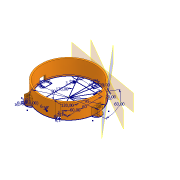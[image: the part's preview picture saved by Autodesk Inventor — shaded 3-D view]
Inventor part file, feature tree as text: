
AUTODESK INVENTOR PART (.ipt)
format: ipt  version: 2020.3 (Build 243373000, 373)  size: 265,216 bytes
history: native  units: mm
features: extrude x8, sketch x5, plane x3
ambient origin geometry x8: Origin, YZ Plane, XZ Plane, XY Plane, X Axis, Y Axis, Z Axis, Center Point
bodies: Body1 (feature_tree)
feature tree (16):
  sketch  "Sketch1"  dims[d0=95.0mm d1=120.0deg]
  extrude  "Extrusion9"  TaperAngle=120.0deg  [1 undecoded]
  extrude  "Extrusion13"  Depth=16.0mm
  extrude  "Extrusion14"  Depth=6.5mm
  extrude  "Extrusion16"  Depth=10.0mm
  extrude  "Extrusion17"  Depth=10.0mm
  plane  "Work Plane5"
  plane  "Work Plane6"
  plane  "Work Plane7"
  sketch  "Sketch12"  dims[d4=3.4mm d5=6.5mm]
  sketch  "Sketch13"  dims[d7=10.0mm d8=3.6mm]
  sketch  "Sketch14"  dims[d9=2.4mm d10=1.2mm d13=30.0mm d15=360.0deg d17=9.8mm d18=12.0mm d19=2.0mm d20=6.0mm d21=2.0mm d23=60.0deg d24=6.1mm d25=8.0mm d26=6.1mm d27=60.0deg d28=3.490659mm d29=3.490659mm d56=40.0mm d57=60.0mm d58=3.2mm d59=1.3mm d60=1.0mm d61=1.0mm d62=1.3mm d64=3.0mm d65=8.0mm d66=6.0mm d74=90.0mm d75=26.0mm d76=0.0mm d83=4.2mm d84=0.0mm d85=8.4mm d86=0.0mm d99=12.5mm d100=0.0mm d101=6.5mm d102=6.0mm d103=6.0mm d104=3.0mm d105=0.0mm d115=4.0mm d116=4.0mm d122=90.0deg d123=90.0deg d124=90.0deg d126=5.5mm d127=5.5mm d128=5.5mm d129=10.0mm d130=0.0mm d131=10.0mm d132=0.0mm d133=10.0mm d134=0.0mm d72=0.5mm d73=0.872665mm d106=0.5mm d107=0.872665mm d108=0.5mm d109=0.872665mm d120=0.5mm d121=0.872665mm d125=0.872665mm]
  extrude  "Extrusion21"  Depth=10.0mm TaperAngle=360.0deg
  extrude  "Extrusion22"  Depth=10.0mm
  extrude  "Extrusion23"  Depth=10.0mm
  sketch  "Sketch8"  dims[d2=120.0deg d3=16.0mm]
note: 1 required parameter value undecoded (feature->parameter linkage not recoverable at this tier; creation-order binding heuristic only, values carry confidence <= 0.55)
